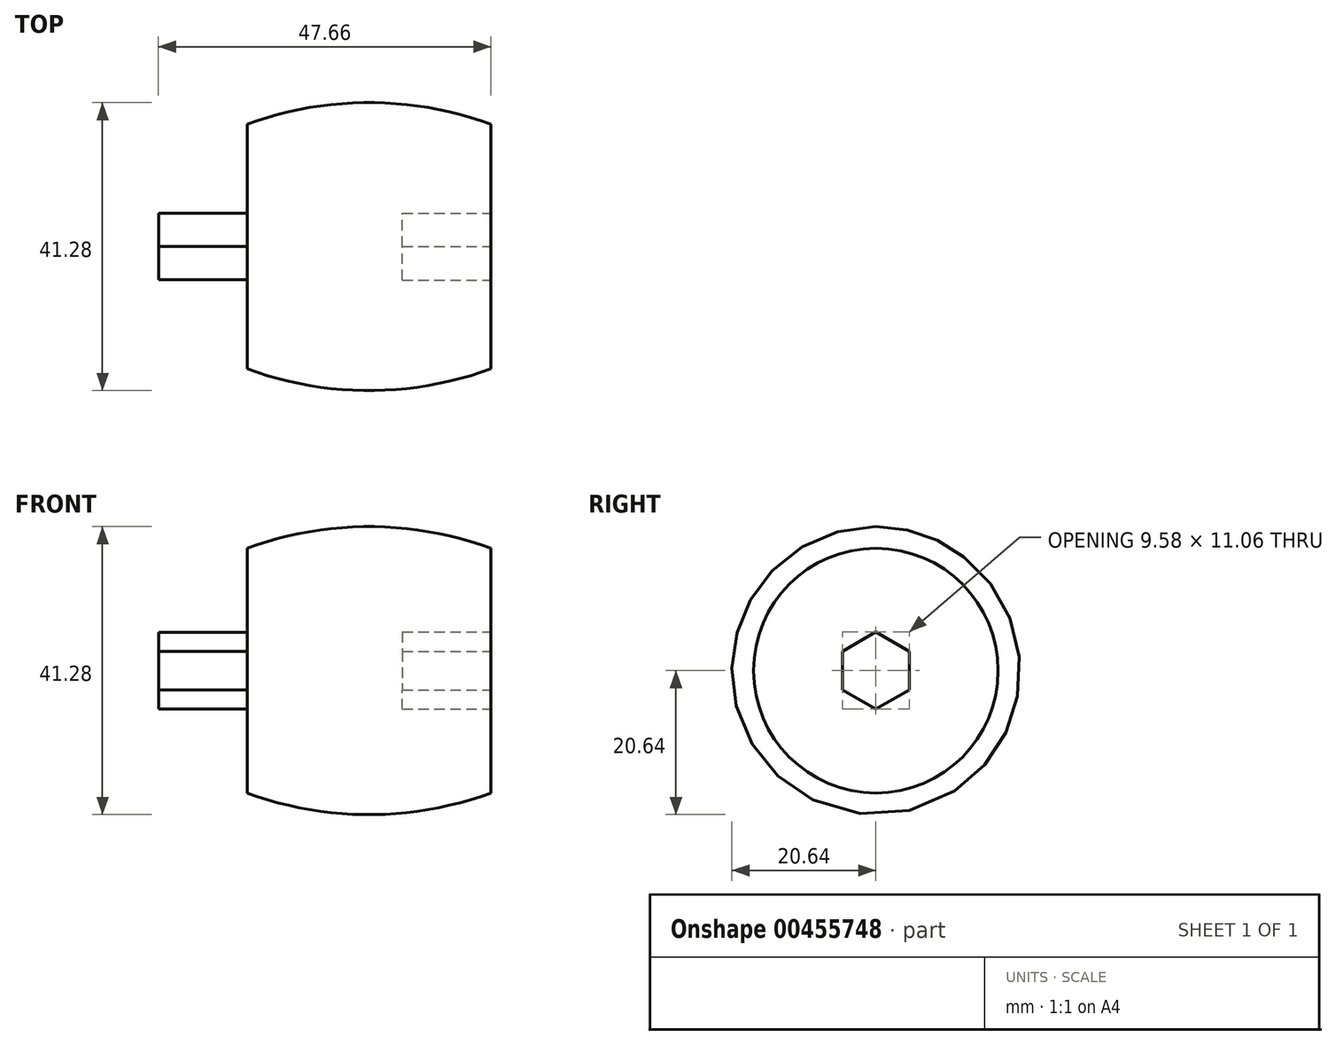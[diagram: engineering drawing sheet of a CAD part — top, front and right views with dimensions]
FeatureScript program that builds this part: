
annotation { "Feature Type Name" : "Feature", "Feature Type Description" : "" }
export const myFeature = defineFeature(function(context is Context, id is Id, definition is map)
    precondition{}
    {
        {
            var Q0;
            Q0=qCreatedBy(makeId("Front.planeOp"),FACE);
            var sketch = newSketch(context, id + "F0", { "sketchPlane" : qUnion([Q0])});
            skArc(sketch, "E0", {"start": v(0, 20.64) * mm, "mid": v(8.87, 19.86) * mm, "end": v(17.48, 17.54) * mm});
            skLineSegment(sketch, "E1", {"start": v(17.48, 17.54) * mm, "end": v(17.48, 0) * mm});
            skLineSegment(sketch, "E2", {"start": v(-66.86, 0) * mm, "end": v(58.05, 0) * mm, "construction": true});
            skLineSegment(sketch, "E3", {"start": v(0, 0) * mm, "end": v(0, 53.96) * mm, "construction": true});
            skArc(sketch, "E4.MirrorCS", {"start": v(0, 20.64) * mm, "mid": v(-8.87, 19.86) * mm, "end": v(-17.48, 17.54) * mm});
            skLineSegment(sketch, "E5.MirrorCS", {"start": v(-17.48, 17.54) * mm, "end": v(-17.48, 0) * mm});
            skLineSegment(sketch, "E6", {"start": v(-17.48, 0) * mm, "end": v(17.48, 0) * mm, "construction": true});
            skLineSegment(sketch, "E7", {"start": v(-17.48, 0) * mm, "end": v(17.48, 0) * mm});
            skSolve(sketch);
        }
        {
            var Q0;
            Q0 = qSketchRegion(id + "F0", true);
            var Q1;
            Q1=sQuery(id+"F0.wireOp",EDGE,"E2");
            revolve(context, id + "F1", {"entities" : qUnion([Q0]), "axis" : qUnion([Q1]), "revolveType" : RevolveType.FULL});
        }
        {
            var Q0;
            Q0=makeQuery(id+"F1.opRevolve","SWEPT_FACE",FACE,{"disambiguationData":[OSD([sQuery(id+"F0.wireOp",EDGE,"E1")])]});
            var sketch = newSketch(context, id + "F2", { "sketchPlane" : qUnion([Q0])});
            skCircle(sketch, "E8.cCircle", {"center": v(0, 0) * mm, "radius": 4.79 * mm, "construction": true});
            skLineSegment(sketch, "E8.0", {"start": v(4.79, 2.76) * mm, "end": v(4.79, -2.76) * mm});
            skLineSegment(sketch, "E8.1", {"start": v(4.79, -2.76) * mm, "end": v(0, -5.53) * mm});
            skLineSegment(sketch, "E8.2", {"start": v(0, -5.53) * mm, "end": v(-4.79, -2.76) * mm});
            skLineSegment(sketch, "E8.3", {"start": v(-4.79, -2.76) * mm, "end": v(-4.79, 2.76) * mm});
            skLineSegment(sketch, "E8.4", {"start": v(-4.79, 2.76) * mm, "end": v(0, 5.53) * mm});
            skLineSegment(sketch, "E8.5", {"start": v(0, 5.53) * mm, "end": v(4.79, 2.76) * mm});
            skPoint(sketch, "E8.0.midPoint", {"position": v(4.79, 0) * mm});
            skSolve(sketch);
        }
        {
            var Q0;
            Q0 = qSketchRegion(id + "F2", true);
            extrude(context, id + "F3", {"entities" : qUnion([Q0]), "operationType" : NewBodyOperationType.REMOVE, "oppositeDirection" : true, "depth" : 12.7 * mm, "offsetDistance" : 25.4 * mm});
        }
        {
            var Q0;
            Q0=makeQuery(id+"F1.opRevolve","SWEPT_FACE",FACE,{"disambiguationData":[OSD([sQuery(id+"F0.wireOp",EDGE,"E5.MirrorCS")])]});
            var sketch = newSketch(context, id + "F4", { "sketchPlane" : qUnion([Q0])});
            skCircle(sketch, "E9.cCircle", {"center": v(0, 0) * mm, "radius": 4.76 * mm, "construction": true});
            skLineSegment(sketch, "E9.0", {"start": v(4.76, 2.75) * mm, "end": v(4.76, -2.75) * mm});
            skLineSegment(sketch, "E9.1", {"start": v(4.76, -2.75) * mm, "end": v(0, -5.5) * mm});
            skLineSegment(sketch, "E9.2", {"start": v(0, -5.5) * mm, "end": v(-4.76, -2.75) * mm});
            skLineSegment(sketch, "E9.3", {"start": v(-4.76, -2.75) * mm, "end": v(-4.76, 2.75) * mm});
            skLineSegment(sketch, "E9.4", {"start": v(-4.76, 2.75) * mm, "end": v(0, 5.5) * mm});
            skLineSegment(sketch, "E9.5", {"start": v(0, 5.5) * mm, "end": v(4.76, 2.75) * mm});
            skPoint(sketch, "E9.0.midPoint", {"position": v(4.76, 0) * mm});
            skSolve(sketch);
        }
        {
            var Q0;
            Q0 = qSketchRegion(id + "F4", true);
            extrude(context, id + "F5", {"entities" : qUnion([Q0]), "operationType" : NewBodyOperationType.ADD, "depth" : 12.7 * mm, "offsetDistance" : 25.4 * mm});
        }
    });
